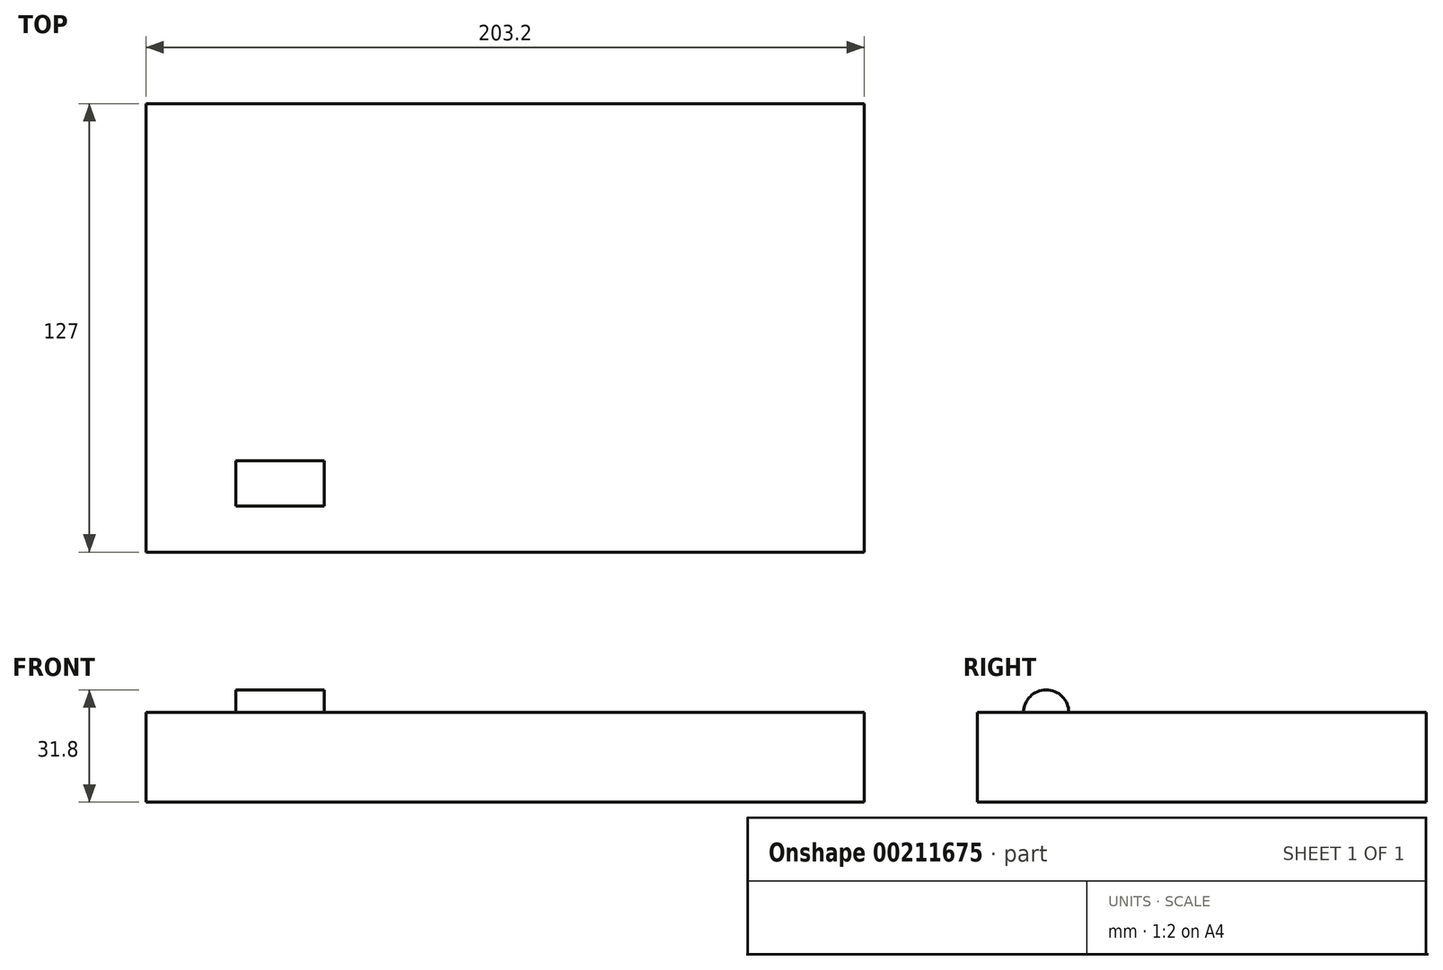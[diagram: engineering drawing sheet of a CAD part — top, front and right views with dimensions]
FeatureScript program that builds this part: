
annotation { "Feature Type Name" : "Feature", "Feature Type Description" : "" }
export const myFeature = defineFeature(function(context is Context, id is Id, definition is map)
    precondition{}
    {
        {
            var Q0;
            Q0=qCreatedBy(makeId("Top.planeOp"),FACE);
            var sketch = newSketch(context, id + "F0", { "sketchPlane" : qUnion([Q0])});
            skLineSegment(sketch, "E0.bottom", {"start": v(-123.18, -61.56) * mm, "end": v(80.02, -61.56) * mm});
            skLineSegment(sketch, "E0.top", {"start": v(-123.18, 65.44) * mm, "end": v(80.02, 65.44) * mm});
            skLineSegment(sketch, "E0.left", {"start": v(-123.18, -61.56) * mm, "end": v(-123.18, 65.44) * mm});
            skLineSegment(sketch, "E0.right", {"start": v(80.02, -61.56) * mm, "end": v(80.02, 65.44) * mm});
            skSolve(sketch);
        }
        {
            var Q0;
            Q0 = qSketchRegion(id + "F0", true);
            extrude(context, id + "F1", {"entities" : qUnion([Q0]), "depth" : 25.4 * mm});
        }
        {
            var Q0;
            Q0=makeQuery(id+"F1.opExtrude","SWEPT_FACE",FACE,{"disambiguationData":[OSD([sQuery(id+"F0.wireOp",EDGE,"E0.left")])]});
            cPlane(context, id + "F2", {"entities" : qUnion([Q0]), "cplaneType" : CPlaneType.OFFSET, "offset" : 25.4 * mm, "oppositeDirection" : true, "width" : 152.4 * mm, "height" : 152.4 * mm});
        }
        {
            var Q0;
            Q0=qCreatedBy(id+"F2.planeOp",FACE);
            var sketch = newSketch(context, id + "F3", { "sketchPlane" : qUnion([Q0])});
            skCircle(sketch, "E1", {"center": v(42.09, 25.4) * mm, "radius": 6.4 * mm});
            skLineSegment(sketch, "E2", {"start": v(62.52, 25.4) * mm, "end": v(-73.65, 25.4) * mm, "construction": true});
            skSolve(sketch);
        }
        {
            var Q0;
            Q0 = qSketchRegion(id + "F3", true);
            var Q1;
            Q1 = qConstructionFilter(qBodyType(qCreatedBy(id + "F3" ,EDGE), BodyType.WIRE), ConstructionObject.NO);
            extrude(context, id + "F4", {"entities" : qUnion([Q0]), "operationType" : NewBodyOperationType.ADD, "surfaceEntities" : qUnion([Q1]), "oppositeDirection" : true, "depth" : 25 * mm});
        }
    });
